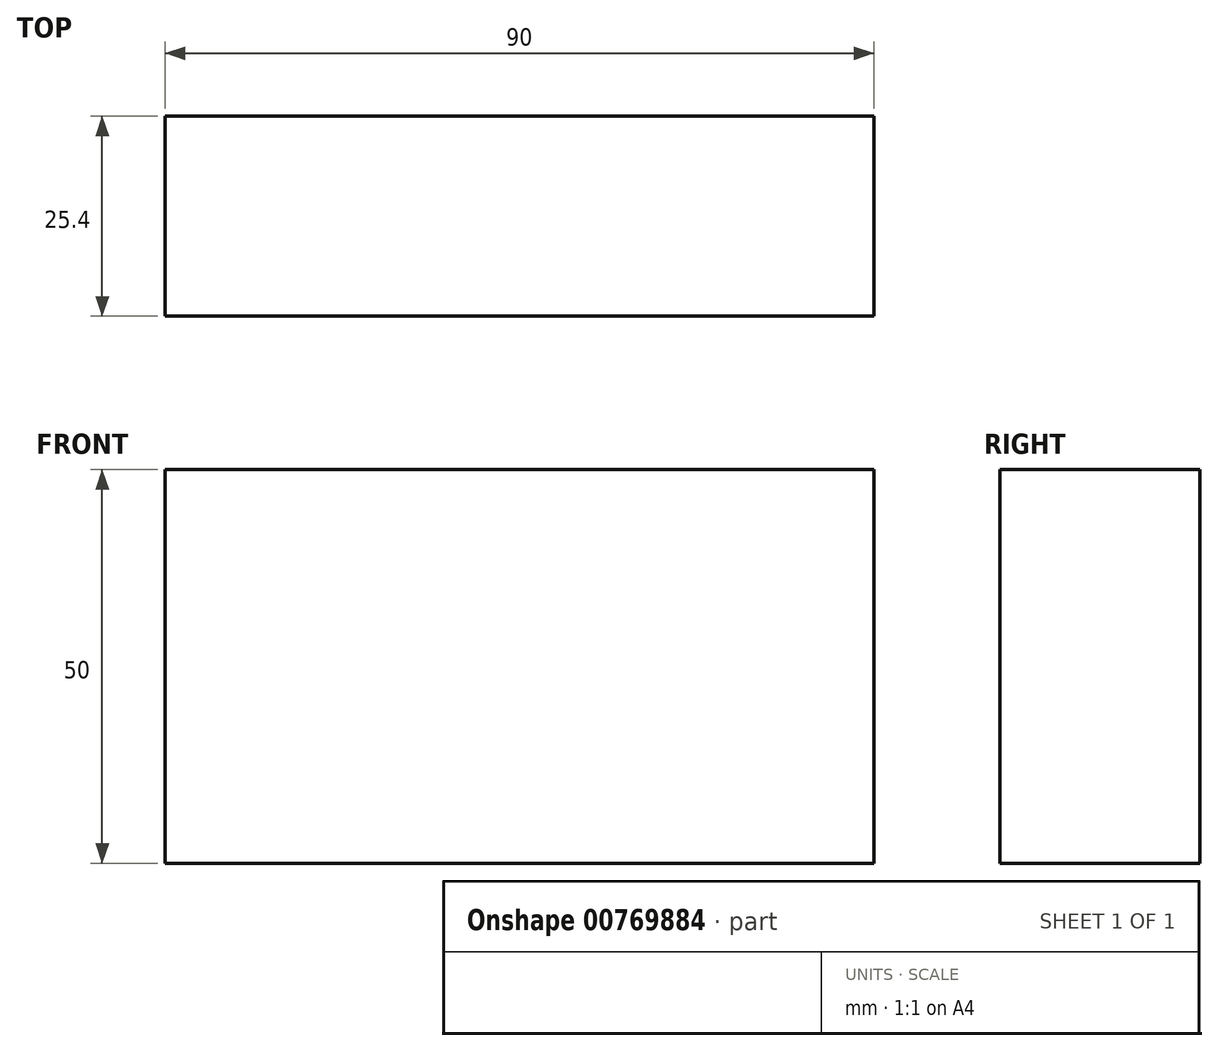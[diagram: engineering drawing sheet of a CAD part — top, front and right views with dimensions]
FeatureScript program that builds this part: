
annotation { "Feature Type Name" : "Feature", "Feature Type Description" : "" }
export const myFeature = defineFeature(function(context is Context, id is Id, definition is map)
    precondition{}
    {
        {
            var Q0;
            Q0=qCreatedBy(makeId("Front.planeOp"),FACE);
            var sketch = newSketch(context, id + "F0", { "sketchPlane" : qUnion([Q0])});
            skLineSegment(sketch, "E0.bottom", {"start": v(0, 0) * mm, "end": v(90, 0) * mm});
            skLineSegment(sketch, "E0.top", {"start": v(0, 50) * mm, "end": v(90, 50) * mm});
            skLineSegment(sketch, "E0.left", {"start": v(0, 0) * mm, "end": v(0, 50) * mm});
            skLineSegment(sketch, "E0.right", {"start": v(90, 0) * mm, "end": v(90, 50) * mm});
            skSolve(sketch);
        }
        {
            var Q0;
            Q0=makeQuery(id+"F0.imprint","IMPRINT",FACE,{"disambiguationData":[TD([[makeQuery(id+"F0.imprint","IMPRINT",EDGE,{"derivedFrom":sQuery(id+"F0.wireOp",EDGE,"E0.bottom")}),1.0]])]});
            extrude(context, id + "F1", {"entities" : qUnion([Q0]), "depth" : 25.4 * mm, "offsetDistance" : 25.4 * mm});
        }
    });
